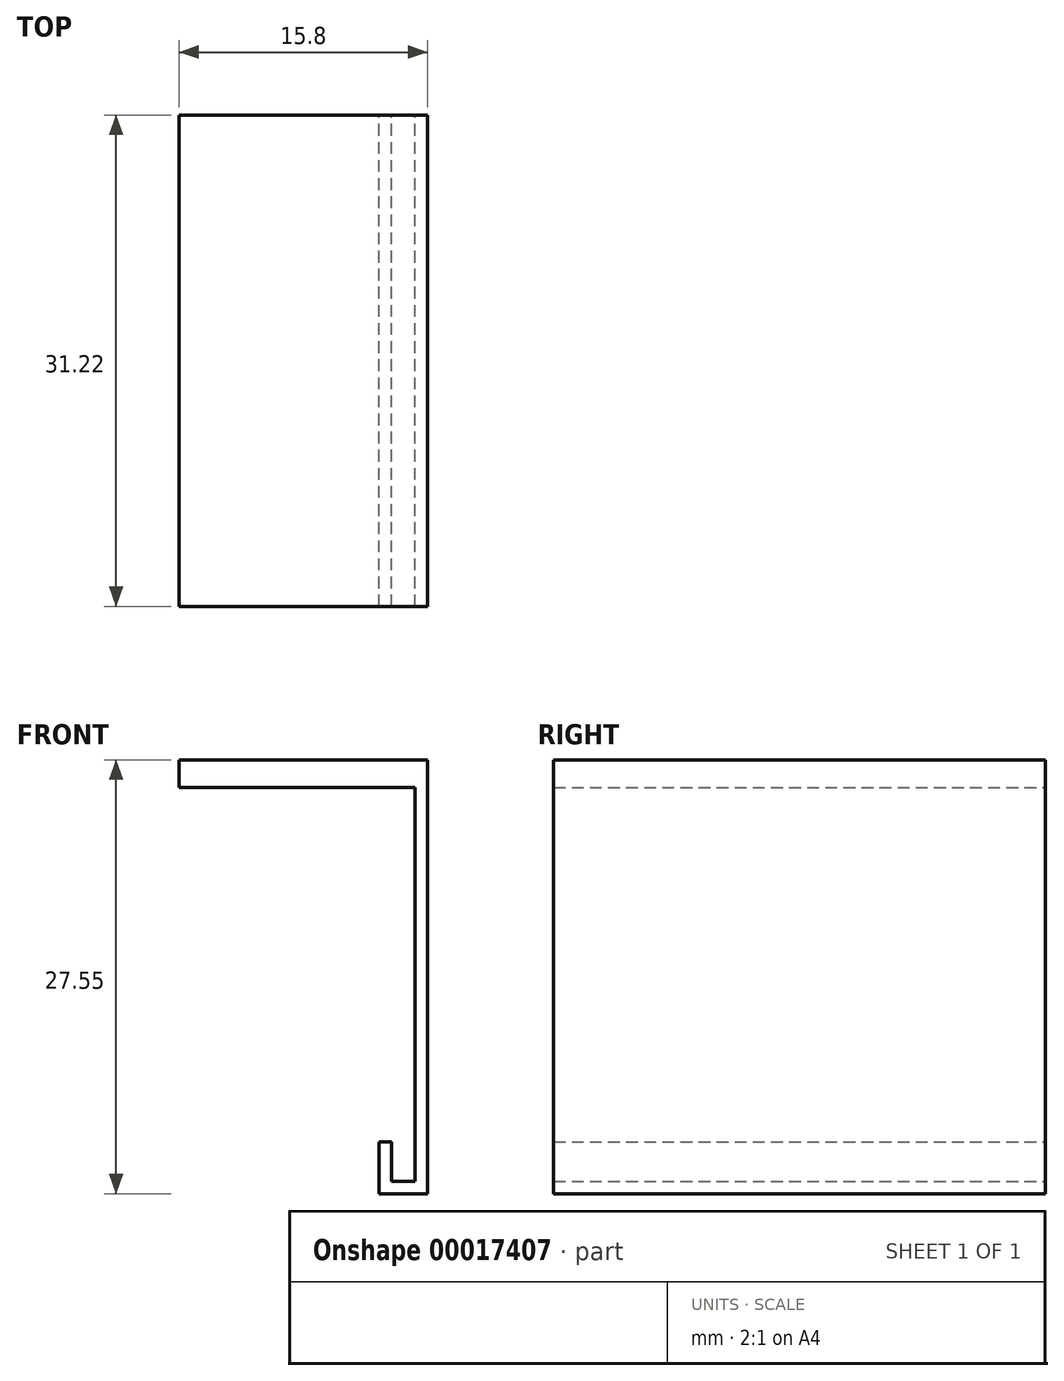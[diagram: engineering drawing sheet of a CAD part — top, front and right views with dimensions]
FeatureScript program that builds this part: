
annotation { "Feature Type Name" : "Feature", "Feature Type Description" : "" }
export const myFeature = defineFeature(function(context is Context, id is Id, definition is map)
    precondition{}
    {
        {
            var Q0;
            Q0=qCreatedBy(makeId("Front.planeOp"),FACE);
            var sketch = newSketch(context, id + "F0", { "sketchPlane" : qUnion([Q0])});
            skLineSegment(sketch, "E0", {"start": v(-21.91, 28.05) * mm, "end": v(-6.91, 28.05) * mm});
            skLineSegment(sketch, "E1", {"start": v(-6.91, 28.05) * mm, "end": v(-6.91, 3.05) * mm});
            skLineSegment(sketch, "E2", {"start": v(-6.91, 3.05) * mm, "end": v(-8.41, 3.05) * mm});
            skLineSegment(sketch, "E3", {"start": v(-8.41, 3.05) * mm, "end": v(-8.41, 5.55) * mm});
            skLineSegment(sketch, "E4", {"start": v(-8.41, 5.55) * mm, "end": v(-9.21, 5.55) * mm});
            skLineSegment(sketch, "E5", {"start": v(-9.21, 5.55) * mm, "end": v(-9.21, 2.25) * mm});
            skLineSegment(sketch, "E6", {"start": v(-9.21, 2.25) * mm, "end": v(-6.11, 2.25) * mm});
            skLineSegment(sketch, "E7", {"start": v(-6.11, 2.25) * mm, "end": v(-6.11, 29.8) * mm});
            skLineSegment(sketch, "E8", {"start": v(-6.11, 29.8) * mm, "end": v(-21.91, 29.8) * mm});
            skLineSegment(sketch, "E9", {"start": v(-21.91, 29.8) * mm, "end": v(-21.91, 28.05) * mm});
            skSolve(sketch);
        }
        {
            var Q0;
            Q0=makeQuery(id+"F0.imprint","IMPRINT",FACE,{"disambiguationData":[TD([[makeQuery(id+"F0.imprint","IMPRINT",EDGE,{"derivedFrom":sQuery(id+"F0.wireOp",EDGE,"E0")}),1.0]])]});
            extrude(context, id + "F1", {"entities" : qUnion([Q0]), "depth" : 31.22 * mm});
        }
    });
